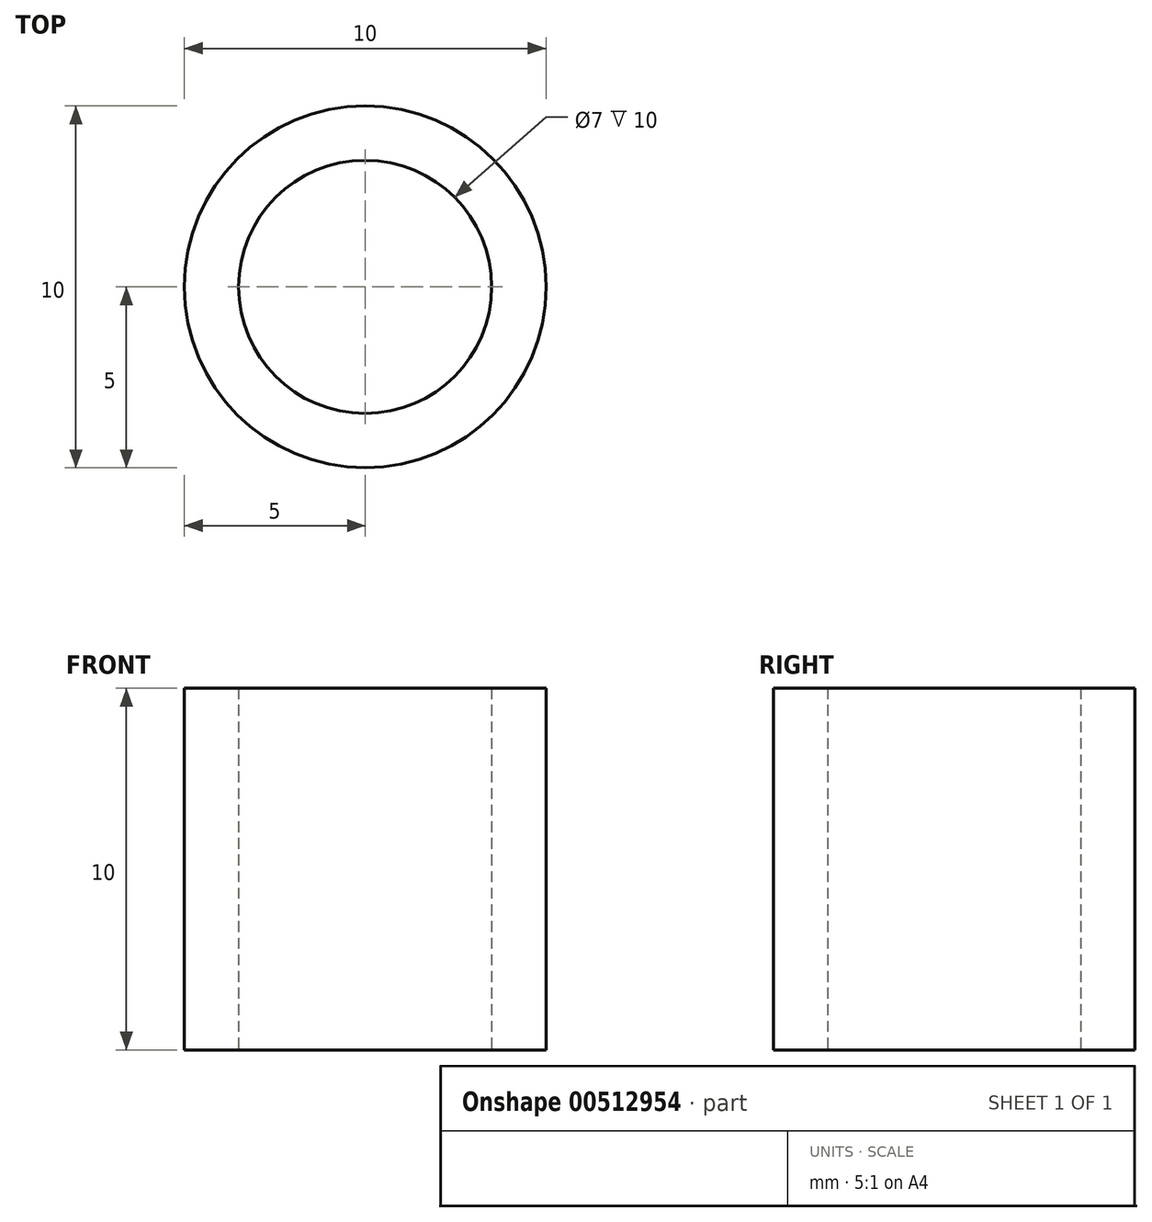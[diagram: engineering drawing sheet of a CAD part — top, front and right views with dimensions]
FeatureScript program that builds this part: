
annotation { "Feature Type Name" : "Feature", "Feature Type Description" : "" }
export const myFeature = defineFeature(function(context is Context, id is Id, definition is map)
    precondition{}
    {
        {
            var Q0;
            Q0=qCreatedBy(makeId("Top.planeOp"),FACE);
            var sketch = newSketch(context, id + "F0", { "sketchPlane" : qUnion([Q0])});
            skCircle(sketch, "E0", {"center": v(0, 0) * mm, "radius": 3.5 * mm});
            skCircle(sketch, "E1", {"center": v(0, 0) * mm, "radius": 5 * mm});
            skSolve(sketch);
        }
        {
            var Q0;
            Q0=makeQuery(id+"F0.imprint","IMPRINT",FACE,{"disambiguationData":[TD([[makeQuery(id+"F0.imprint","IMPRINT",EDGE,{"derivedFrom":sQuery(id+"F0.wireOp",EDGE,"E0")}),-1.0]])]});
            extrude(context, id + "F1", {"entities" : qUnion([Q0]), "depth" : 10 * mm, "offsetDistance" : 25 * mm});
        }
    });
